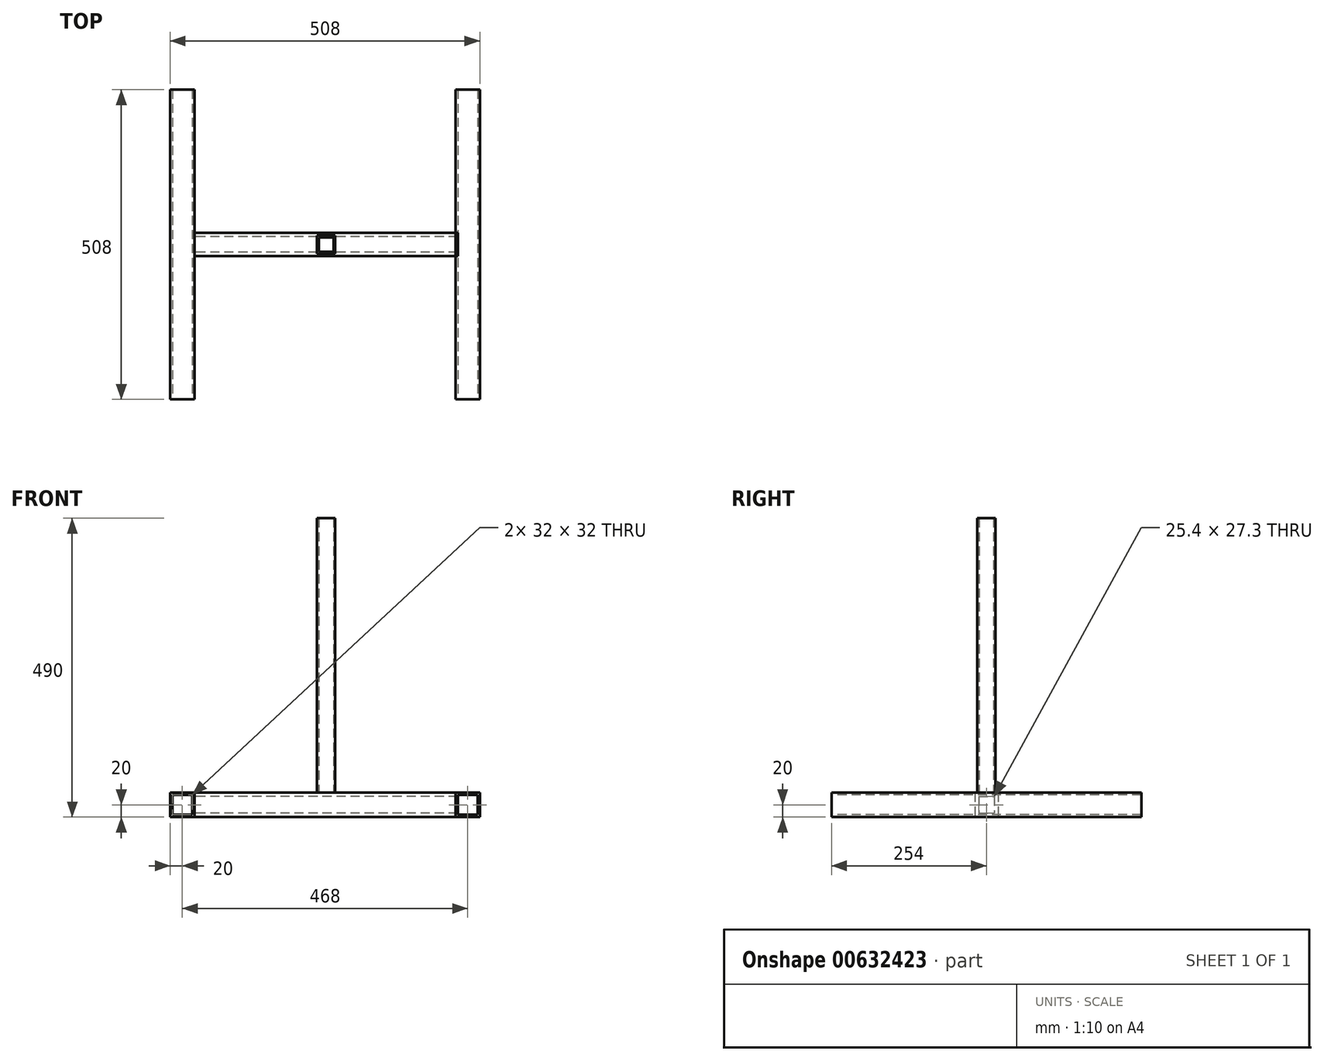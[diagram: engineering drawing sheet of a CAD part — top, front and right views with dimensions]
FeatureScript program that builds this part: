
annotation { "Feature Type Name" : "Feature", "Feature Type Description" : "" }
export const myFeature = defineFeature(function(context is Context, id is Id, definition is map)
    precondition{}
    {
        {
            var Q0;
            Q0=qCreatedBy(makeId("Front.planeOp"),FACE);
            var sketch = newSketch(context, id + "F0", { "sketchPlane" : qUnion([Q0])});
            skLineSegment(sketch, "E0.bottom", {"start": v(-254, 0) * mm, "end": v(-214, 0) * mm});
            skLineSegment(sketch, "E0.top", {"start": v(-254, 40) * mm, "end": v(-214, 40) * mm});
            skLineSegment(sketch, "E0.left", {"start": v(-254, 0) * mm, "end": v(-254, 40) * mm});
            skLineSegment(sketch, "E0.right", {"start": v(-214, 0) * mm, "end": v(-214, 40) * mm});
            skLineSegment(sketch, "E1.0", {"start": v(-250, 36) * mm, "end": v(-218, 36) * mm});
            skLineSegment(sketch, "E1.1", {"start": v(-250, 4) * mm, "end": v(-250, 36) * mm});
            skLineSegment(sketch, "E1.2", {"start": v(-250, 4) * mm, "end": v(-218, 4) * mm});
            skLineSegment(sketch, "E1.3", {"start": v(-218, 4) * mm, "end": v(-218, 36) * mm});
            skLineSegment(sketch, "E2", {"start": v(0, 0) * mm, "end": v(0, 70.33) * mm, "construction": true});
            skLineSegment(sketch, "E3.MirrorCS", {"start": v(250, 4) * mm, "end": v(218, 4) * mm});
            skLineSegment(sketch, "E4.MirrorCS", {"start": v(250, 36) * mm, "end": v(218, 36) * mm});
            skLineSegment(sketch, "E5.MirrorCS", {"start": v(218, 4) * mm, "end": v(218, 36) * mm});
            skLineSegment(sketch, "E6.MirrorCS", {"start": v(254, 40) * mm, "end": v(214, 40) * mm});
            skLineSegment(sketch, "E7.MirrorCS", {"start": v(254, 0) * mm, "end": v(254, 40) * mm});
            skLineSegment(sketch, "E8.MirrorCS", {"start": v(214, 0) * mm, "end": v(214, 40) * mm});
            skLineSegment(sketch, "E9.MirrorCS", {"start": v(254, 0) * mm, "end": v(214, 0) * mm});
            skLineSegment(sketch, "E10.MirrorCS", {"start": v(250, 4) * mm, "end": v(250, 36) * mm});
            skSolve(sketch);
        }
        {
            var Q0;
            Q0=makeQuery(id+"F0.imprint","IMPRINT",FACE,{"disambiguationData":[TD([[makeQuery(id+"F0.imprint","IMPRINT",EDGE,{"derivedFrom":sQuery(id+"F0.wireOp",EDGE,"E0.bottom")}),1.0]])]});
            var Q1;
            Q1=makeQuery(id+"F0.imprint","IMPRINT",FACE,{"disambiguationData":[TD([[makeQuery(id+"F0.imprint","IMPRINT",EDGE,{"derivedFrom":sQuery(id+"F0.wireOp",EDGE,"E3.MirrorCS")}),1.0]])]});
            extrude(context, id + "F1", {"entities" : qUnion([Q0, Q1]), "oppositeDirection" : true, "depth" : 508 * mm, "offsetDistance" : 25 * mm});
        }
        {
            var Q0;
            Q0=makeQuery(id+"F1.opExtrude","SWEPT_FACE",FACE,{"disambiguationData":[OSD([sQuery(id+"F0.wireOp",EDGE,"E0.right")])]});
            var sketch = newSketch(context, id + "F2", { "sketchPlane" : qUnion([Q0])});
            skLineSegment(sketch, "E11", {"start": v(254, 40) * mm, "end": v(254, 0) * mm, "construction": true});
            skLineSegment(sketch, "E12.bottom", {"start": v(234.95, 40) * mm, "end": v(273.05, 40) * mm});
            skLineSegment(sketch, "E12.top", {"start": v(234.95, 0) * mm, "end": v(273.05, 0) * mm});
            skLineSegment(sketch, "E12.left", {"start": v(234.95, 40) * mm, "end": v(234.95, 0) * mm});
            skLineSegment(sketch, "E12.right", {"start": v(273.05, 40) * mm, "end": v(273.05, 0) * mm});
            skLineSegment(sketch, "E13.0", {"start": v(241.3, 33.65) * mm, "end": v(266.7, 33.65) * mm});
            skLineSegment(sketch, "E13.1", {"start": v(241.3, 33.65) * mm, "end": v(241.3, 6.35) * mm});
            skLineSegment(sketch, "E13.2", {"start": v(241.3, 6.35) * mm, "end": v(266.7, 6.35) * mm});
            skLineSegment(sketch, "E13.3", {"start": v(266.7, 33.65) * mm, "end": v(266.7, 6.35) * mm});
            skSolve(sketch);
        }
        {
            var Q0;
            Q0=makeQuery(id+"F2.imprint","IMPRINT",FACE,{"disambiguationData":[TD([[makeQuery(id+"F2.imprint","IMPRINT",EDGE,{"derivedFrom":sQuery(id+"F2.wireOp",EDGE,"E12.bottom")}),1.0]])]});
            extrude(context, id + "F3", {"entities" : qUnion([Q0]), "depth" : 431.8 * mm, "offsetDistance" : 25 * mm});
        }
        {
            var Q0;
            Q0=makeQuery(id+"F3.opExtrude","SWEPT_FACE",FACE,{"disambiguationData":[OSD([sQuery(id+"F2.wireOp",EDGE,"E12.bottom")])]});
            var sketch = newSketch(context, id + "F4", { "sketchPlane" : qUnion([Q0])});
            skLineSegment(sketch, "E14", {"start": v(1.9, 273.05) * mm, "end": v(1.9, 234.95) * mm, "construction": true});
            skLineSegment(sketch, "E15", {"start": v(-23, 254) * mm, "end": v(28.6, 254) * mm, "construction": true});
            skPoint(sketch, "E15.startSnap0", {"position": v(1.9, 254) * mm});
            skLineSegment(sketch, "E16.bottom", {"start": v(-13.1, 269) * mm, "end": v(16.9, 269) * mm});
            skLineSegment(sketch, "E16.top", {"start": v(-13.1, 239) * mm, "end": v(16.9, 239) * mm});
            skLineSegment(sketch, "E16.left", {"start": v(-13.1, 269) * mm, "end": v(-13.1, 239) * mm});
            skLineSegment(sketch, "E16.right", {"start": v(16.9, 269) * mm, "end": v(16.9, 239) * mm});
            skLineSegment(sketch, "E17.0", {"start": v(-10.1, 266) * mm, "end": v(13.9, 266) * mm});
            skLineSegment(sketch, "E17.1", {"start": v(-10.1, 266) * mm, "end": v(-10.1, 242) * mm});
            skLineSegment(sketch, "E17.2", {"start": v(-10.1, 242) * mm, "end": v(13.9, 242) * mm});
            skLineSegment(sketch, "E17.3", {"start": v(13.9, 266) * mm, "end": v(13.9, 242) * mm});
            skSolve(sketch);
        }
        {
            var Q0;
            Q0=makeQuery(id+"F4.imprint","IMPRINT",FACE,{"disambiguationData":[TD([[makeQuery(id+"F4.imprint","IMPRINT",EDGE,{"derivedFrom":sQuery(id+"F4.wireOp",EDGE,"E16.bottom")}),-1.0]])]});
            extrude(context, id + "F5", {"entities" : qUnion([Q0]), "depth" : 450 * mm, "offsetDistance" : 25 * mm});
        }
    });
